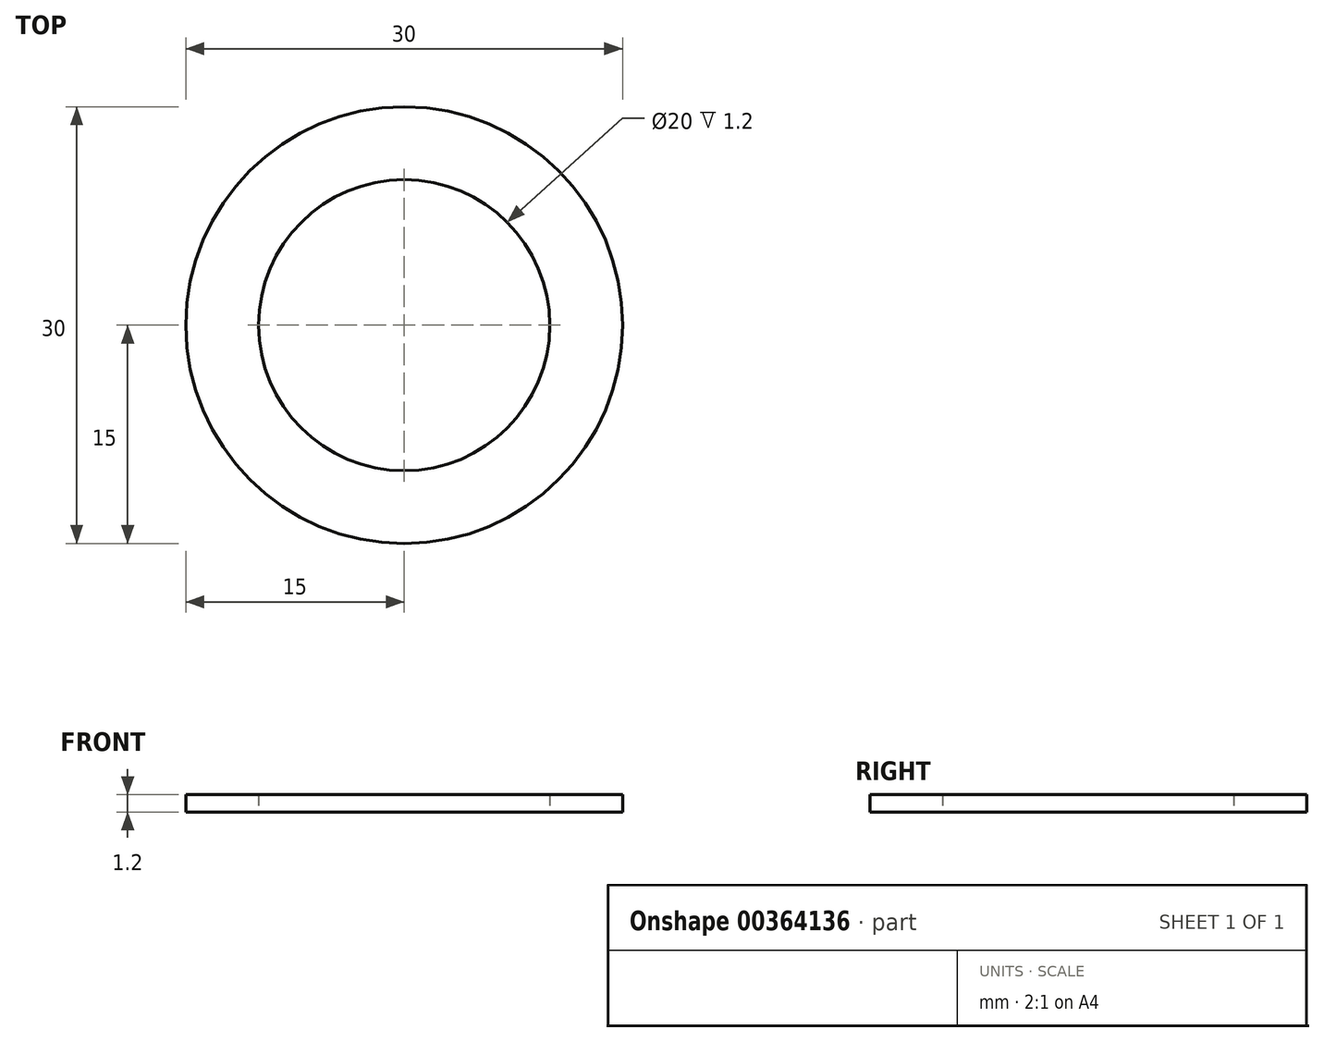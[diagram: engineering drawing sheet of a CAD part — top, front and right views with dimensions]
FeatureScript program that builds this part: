
annotation { "Feature Type Name" : "Feature", "Feature Type Description" : "" }
export const myFeature = defineFeature(function(context is Context, id is Id, definition is map)
    precondition{}
    {
        {
            var Q0;
            Q0=qCreatedBy(makeId("Top.planeOp"),FACE);
            var sketch = newSketch(context, id + "F0", { "sketchPlane" : qUnion([Q0])});
            skLineSegment(sketch, "E0.bottom", {"start": v(25, -25) * mm, "end": v(-25, -25) * mm});
            skLineSegment(sketch, "E0.top", {"start": v(25, 25) * mm, "end": v(-25, 25) * mm});
            skLineSegment(sketch, "E0.left", {"start": v(25, -25) * mm, "end": v(25, 25) * mm});
            skLineSegment(sketch, "E0.right", {"start": v(-25, -25) * mm, "end": v(-25, 25) * mm});
            skPoint(sketch, "E0.middle", {"position": v(0, 0) * mm});
            skLineSegment(sketch, "E1.bottom", {"start": v(20, -20) * mm, "end": v(-20, -20) * mm});
            skLineSegment(sketch, "E1.top", {"start": v(20, 20) * mm, "end": v(-20, 20) * mm});
            skLineSegment(sketch, "E1.left", {"start": v(20, -20) * mm, "end": v(20, 20) * mm});
            skLineSegment(sketch, "E1.right", {"start": v(-20, -20) * mm, "end": v(-20, 20) * mm});
            skCircle(sketch, "E2", {"center": v(0, 0) * mm, "radius": 15 * mm});
            skCircle(sketch, "E3", {"center": v(0, 0) * mm, "radius": 10 * mm});
            skSolve(sketch);
        }
        {
            var Q0;
            Q0=makeQuery(id+"F0.imprint","IMPRINT",FACE,{"disambiguationData":[TD([[makeQuery(id+"F0.imprint","IMPRINT",EDGE,{"derivedFrom":sQuery(id+"F0.wireOp",EDGE,"E2")}),1.0]])]});
            extrude(context, id + "F1", {"entities" : qUnion([Q0]), "depth" : 1.2 * mm});
        }
    });
